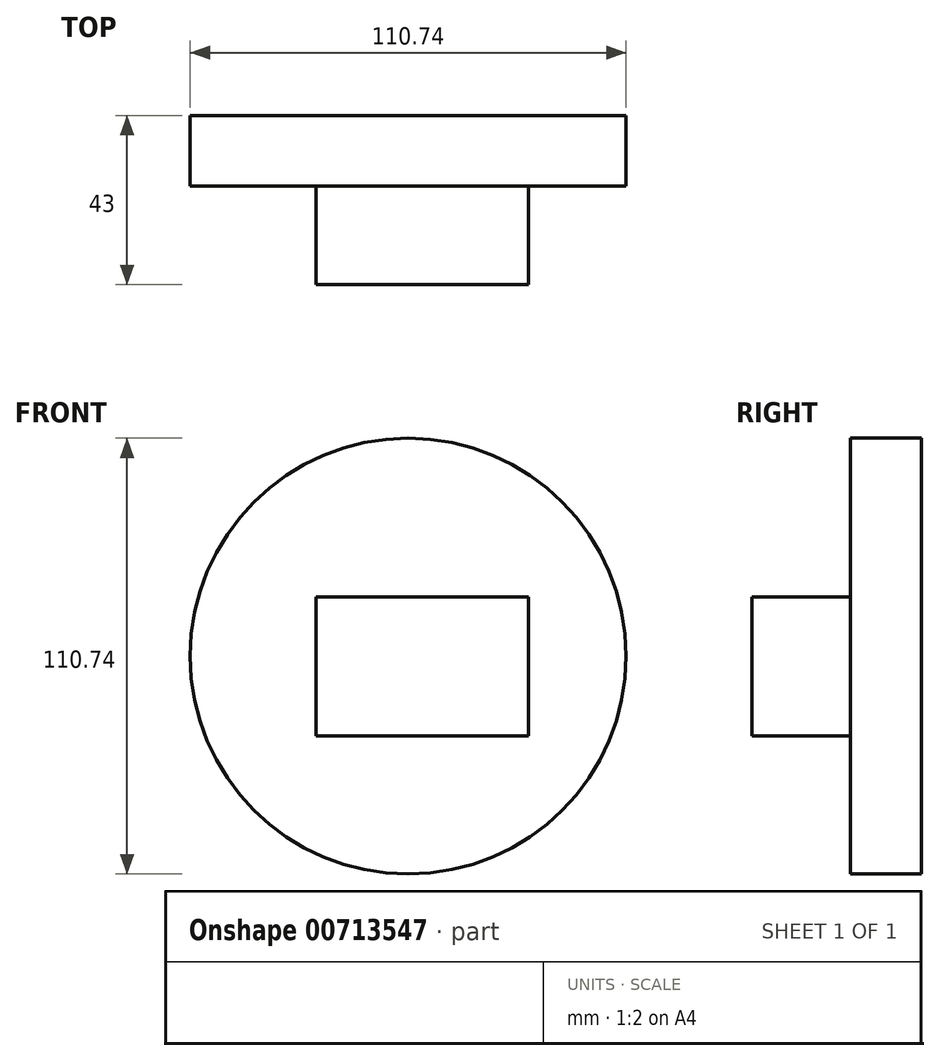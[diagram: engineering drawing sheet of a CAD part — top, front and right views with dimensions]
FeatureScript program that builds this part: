
annotation { "Feature Type Name" : "Feature", "Feature Type Description" : "" }
export const myFeature = defineFeature(function(context is Context, id is Id, definition is map)
    precondition{}
    {
        {
            var Q0;
            Q0=qCreatedBy(makeId("Front.planeOp"),FACE);
            var sketch = newSketch(context, id + "F0", { "sketchPlane" : qUnion([Q0])});
            skCircle(sketch, "E0", {"center": v(0, 0) * mm, "radius": 55.37 * mm});
            skSolve(sketch);
        }
        {
            var Q0;
            Q0=makeQuery(id+"F0.imprint","IMPRINT",FACE,{"disambiguationData":[TD([[makeQuery(id+"F0.imprint","IMPRINT",EDGE,{"derivedFrom":sQuery(id+"F0.wireOp",EDGE,"E0")}),1.0]])]});
            extrude(context, id + "F1", {"entities" : qUnion([Q0]), "depth" : 18 * mm, "offsetDistance" : 25 * mm});
        }
        {
            var Q0;
            Q0=makeQuery(id+"F1.opExtrude","CAP_FACE",FACE,{"disambiguationData":[OSD([sQuery(id+"F0.wireOp",EDGE,"E0")])],"isStart":false});
            var sketch = newSketch(context, id + "F2", { "sketchPlane" : qUnion([Q0])});
            skLineSegment(sketch, "E1.bottom", {"start": v(-23.4, 15.04) * mm, "end": v(30.54, 15.04) * mm});
            skLineSegment(sketch, "E1.top", {"start": v(-23.4, -20.3) * mm, "end": v(30.54, -20.3) * mm});
            skLineSegment(sketch, "E1.left", {"start": v(-23.4, 15.04) * mm, "end": v(-23.4, -20.3) * mm});
            skLineSegment(sketch, "E1.right", {"start": v(30.54, 15.04) * mm, "end": v(30.54, -20.3) * mm});
            skSolve(sketch);
        }
        {
            var Q0;
            Q0 = qSketchRegion(id + "F2", true);
            extrude(context, id + "F3", {"entities" : qUnion([Q0]), "operationType" : NewBodyOperationType.ADD, "depth" : 25 * mm, "offsetDistance" : 25 * mm});
        }
    });
